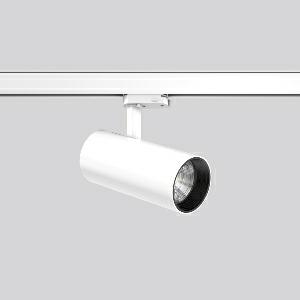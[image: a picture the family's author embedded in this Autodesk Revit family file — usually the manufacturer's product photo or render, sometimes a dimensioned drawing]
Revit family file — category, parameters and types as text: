
# Revit family: deecos_s_mini_742199_002_2_415a
name_source: partatom
category: Lighting Fixtures
units: mm (PartAtom-declared; Revit-internal decimal feet)

## family parameters
Cut with Voids When Loaded = No
Host = Face
Light Source = No
Part Type = Normal
Room Calculation Point = No
Round Connector Dimension = Use Diameter
Shared = No

## types (1)
- DEECOS S mini (1 x LED Modul 927, 2000 lm, 2700)
    Apparent Load = 20 VA
    Approval mark = CE
    CIE Flux Codes = 96 100 100 100 100
    Color Rendering = 92
    Color Temperature = 2700
    Default Elevation = 1800 mm
    Description = Series: DEECOS S mini
LED surface-mounted projector in modern design with no visible cooling ribs. Housing: die-cast aluminium, powder-coated. Rotation range: 356°. Swivel range: 90°. Black plastic ring and recessed LED to prevent glare from the side. Optical assembly with lens made of plastic (polycarbonate) for the best homogeneous light distribution - can be changed without tools. Best colour rendering index Ra>90. With multi adaptor for 3-circuit tracks 230 V. Suitable for Track on ceiling, Wall track. High quality converter without flickering and stroboscopic effect. The following accessories can be mounted without use of tools: interchangeable lenses, decorative glasses, honeycomb louvre, clear and frosted diffusers, white interchangeable plastic ring. 
Colour: traffic white, matt (RAL 9016)
Diameter: 87 mm
Height: 214 mm
Lamp: LED
Socket: without socket
Colour temperature: 2700K
Colour rendering index (CRI): 92
System power: 20 W
Rated luminous flux: 2000 lm
Luminous efficiency: 100 lm/W
Control gear: Regulated power supply
Protection class: I
Type of protection: IP 20
    Height = 214 mm
    Lamp = 1 x LED Modul 927
    Lamp Light Flux = 2000 lm
    Lamp count = 1
    Length = 87 mm
    Lifetime = 50000 h
    Luminous efficacy = 100 lm/W
    Manufacturer = RZB
    ModVariant = No
    Model = 742199.002.2
    Mounting Place = Ceiling
    Mounting Type = Rail mounted
    Number of Poles = 1
    OnlyDefault = Yes
    Power Factor = 1
    Product Name = DEECOS S mini
    Product group = Track mounted projectors
    ProductGroupID = 301
    Protection Class = Protection class I
    Protection Degree = IP 20
    RLX_Detail_Level = 1
    RLX_Emergency_Light_Flux = 0 lm
    RLX_Emergency_Type = 0
    RLX_Emergency_Type_DB = No
    RlxData = <blob elided: 35029 chars, md5=af6b1fd7>
    Socket = socket
    Standby Power = 0 W
    System Light Flux = 2000 lm
    System Power = 20 W
    Type Comments = Product without accessories
    Type Image = 741930.002.jpg
    URL = http://relux.com
    VarID = ---
    Voltage = 230 V
    Voltage Range = 220-240 V
    Weight = 0.00 kg
    Width = 0 mm  [stored 0 ft]

note: [stored X ft] marks values corroborated as IEEE doubles in the binary element streams (Revit-internal decimal feet)

## geometry (parser evidence)
native form markers: Blend x4, Sweep x12
no freeform markers — native parametric forms only
